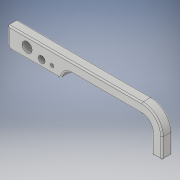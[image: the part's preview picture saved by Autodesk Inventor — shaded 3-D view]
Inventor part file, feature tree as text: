
AUTODESK INVENTOR PART (.ipt)
format: ipt  version: 2019.4 (Build 234330000, 330)  size: 173,056 bytes
history: native  units: mm
features: fillet x5, extrude x2, sketch x2, other x1
ambient origin geometry x8: Origin, YZ Plane, XZ Plane, XY Plane, X Axis, Y Axis, Z Axis, Center Point
bodies: Body1 (feature_tree)
feature tree (10):
  other  "Sólido1"
  extrude  "Extrusión1"  Depth=6000.0mm
  fillet  "Empalme1"  Radius=20000.0mm
  extrude  "Extrusión2"  Depth=3000.0mm
  fillet  "Empalme2"  Radius=1500.0mm
  fillet  "Empalme3"  Radius=500.0mm
  fillet  "Empalme4"  Radius=500.0mm
  fillet  "Empalme5"  Radius=1000.0mm
  sketch  "Boceto1"  dims[d4=3000.0mm d5=6000.0mm d7=20000.0mm]
  sketch  "Boceto2"  dims[d8=8000.0mm d10=3000.0mm d11=1500.0mm d12=0.0mm d13=500.0mm d14=500.0mm d15=1000.0mm d16=1500.0mm d17=1500.0mm d18=0.0mm d19=500.0mm d20=200.0mm d21=200.0mm d22=200.0mm]
